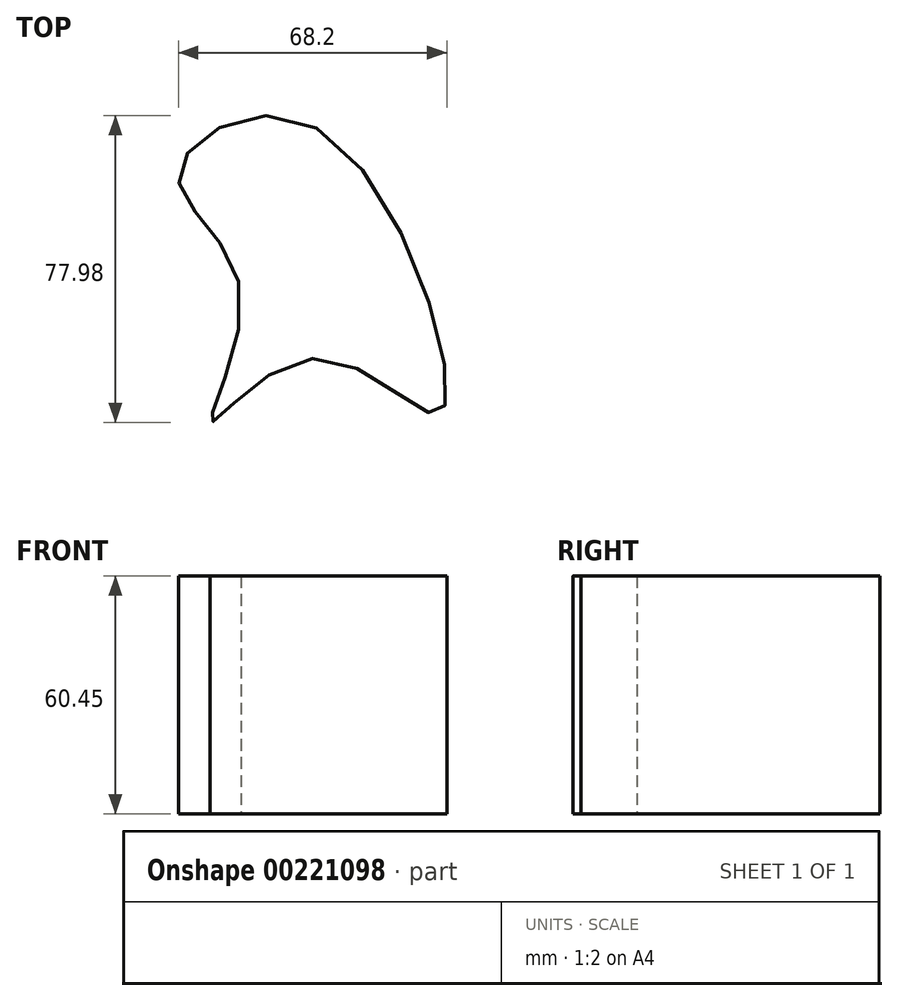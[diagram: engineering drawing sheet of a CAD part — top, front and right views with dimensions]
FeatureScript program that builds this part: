
annotation { "Feature Type Name" : "Feature", "Feature Type Description" : "" }
export const myFeature = defineFeature(function(context is Context, id is Id, definition is map)
    precondition{}
    {
        {
            var Q0;
            Q0=qCreatedBy(makeId("Top.planeOp"),FACE);
            var sketch = newSketch(context, id + "F0", { "sketchPlane" : qUnion([Q0])});
            skFitSpline(sketch, "E0", {"points": [v(0, 40.57) * mm, v(-35.01, 29.09) * mm, v(-19.45, 0) * mm, v(-26.86, -34.27) * mm, v(0, -17.97) * mm, v(31.68, -31.68) * mm, v(0, 40.57) * mm]});
            skSolve(sketch);
        }
        {
            var Q0;
            Q0=makeQuery(id+"F0.imprint","IMPRINT",FACE,{"disambiguationData":[TD([[makeQuery(id+"F0.imprint","IMPRINT",EDGE,{"derivedFrom":sQuery(id+"F0.wireOp",EDGE,"E0")}),1.0]])]});
            extrude(context, id + "F1", {"entities" : qUnion([Q0]), "depth" : 60.45 * mm});
        }
    });
